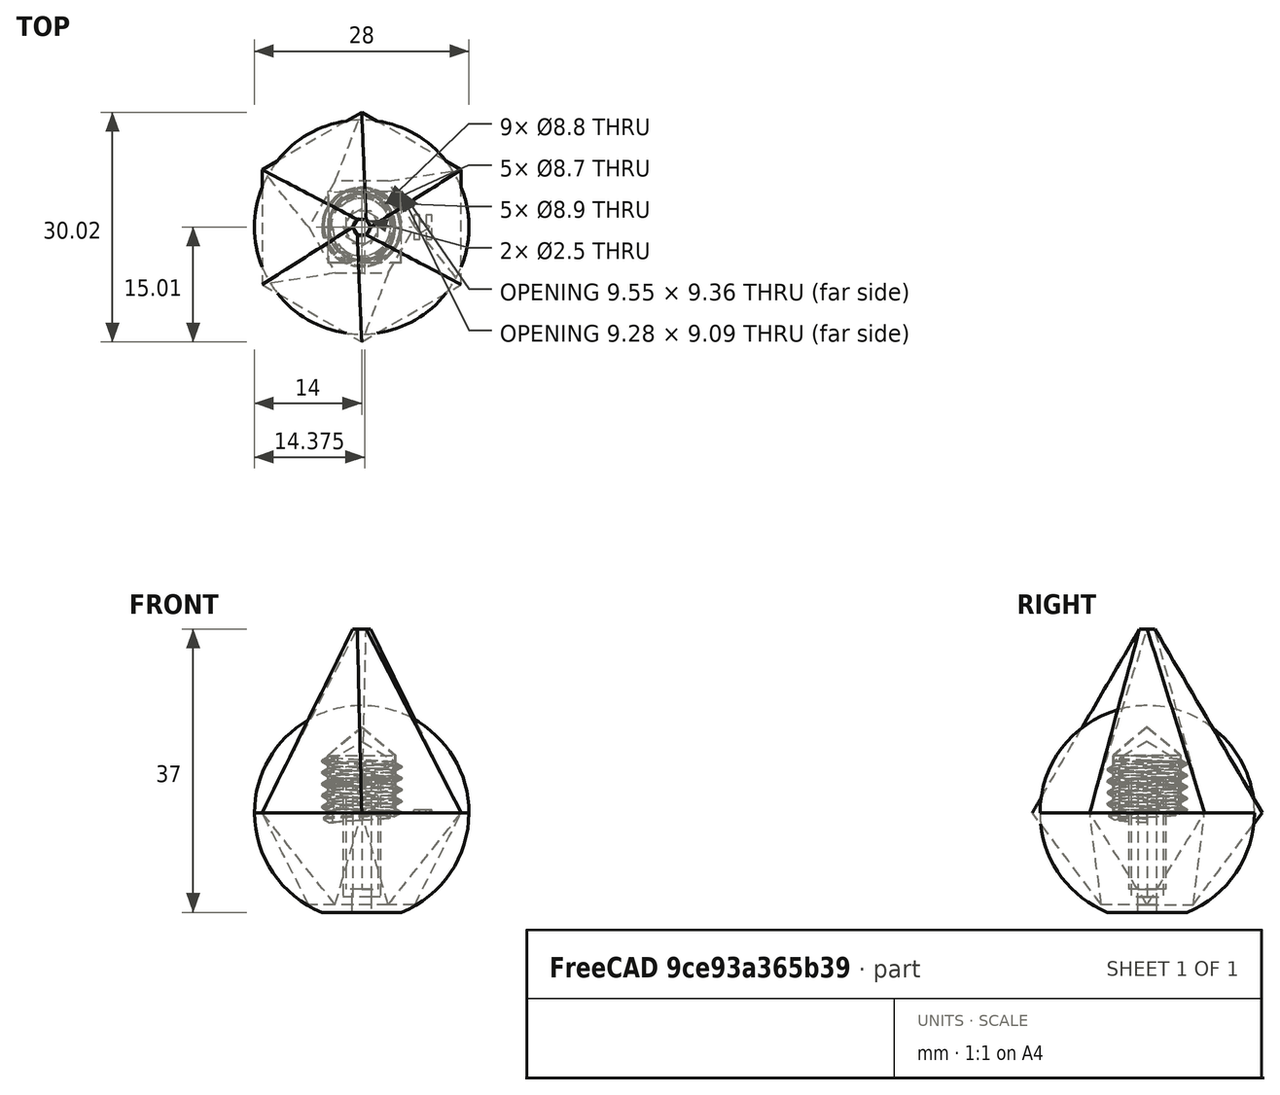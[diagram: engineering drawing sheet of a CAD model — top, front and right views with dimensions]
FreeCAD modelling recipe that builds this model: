
FCSTD DOCUMENT  (FreeCAD 2022.111R28429 (Git))
Label: Spec_PB3D_Tail_FCLinkBranch
License: All rights reserved
LicenseURL: http://en.wikipedia.org/wiki/All_rights_reserved
objects: Sketcher::SketchObject×23, PartDesign::Body×8, PartDesign::Hole×6, PartDesign::Pocket×6, PartDesign::Plane×4, PartDesign::AdditiveLoft×4, PartDesign::Revolution×2, PartDesign::Pad×2, PartDesign::SubShapeBinder×2, PartDesign::Boolean×2, PartDesign::Groove×2, App::Part×2, Mesh::Feature×2, Spreadsheet::Sheet×1
note: 107 computed .brp shape members not serialized (recipe doc carries the construction recipe); baked Part::Feature solids carry a one-line shape summary decoded from their .brp

FEATURE [Spreadsheet::Sheet] Spreadsheet  label="params"
  PythonMode = false
  ShowCells = 0
  TreeRank = 1
  cells = A1=M2 Bolt Clearances; C1=M2.5 Bolt Clearances; E1=Std Dims; G1=Clip; A2=Hole Clear Diam; B2(m2_hole_clear_diam)==2.5mm; C2=Hole Clear Diam; D2(m25_hole_clear_diam)==2.8mm; E2=Std. Chamfer; F2(std_chamf)==1mm; G2=Clip Tol; H2(clip_tol)==0.15mm; A3=Head Clear Diam; B3(m2_head_clear_diam)==4mm; C3=Head Clear Diam; D3(m25_head_clear_diam)==5mm; E3=Std. Radius; F3(std_rad)==2mm; A4=Head Min Depth; B4(m2_head_min_depth)==1.3mm; C4=Head Min Depth; D4(m25_head_min_depth)==1.6mm; G4=Clip Wall Thick; H4(clip_wall_thick)==0.8mm; A5=Nut Clear Flat; B5(m2_nut_clear_flat)==4.2mm; C5=Nut Clear Flat; D5(m25_nut_clear_flat)==5.2mm; G5=Clip Ball Diam; H5(clip_ball_diam)==0.5mm; A6=Nut Min Depth; B6(m2_nut_min_depth)==1.75mm; C6=Nut Min Depth; D6(m25_nut_min_depth)==2mm; G6=Clip Slot Width; H6(clip_slot_width)==clip_inner_diam / 2; G7=Clip Chamf; H7(clip_chamf)==1mm; A8=Tail Dims; C8=Base Plate Dims; A9=Tail Tot Height; B9(tail_tot_height)==tail_base_height + tail_top_height; C9=Base Plate Outer Diam; D9(base_plate_outer_diam)==9.4mm; G9=Clip Inner Diam; H9(clip_inner_diam)==5mm; A10=Tail Base Height; B10(tail_base_height)==12mm; C10=Base Plate Inner Diam; D10(base_plate_inner_diam)==4.8mm; G10=Clip Outer Diam; H10(clip_outer_diam)==clip_inner_diam + 2 * clip_wall_thick; A11=Tail Top Height; B11(tail_top_height)==24mm; C11=Base Plate Thick; D11(base_plate_thick)==1.2mm; G11=Clip Height; H11(clip_height)==clip_ball_diam + clip_chamf + 3mm; A12=Tail Base Width; B12(tail_base_width)==12mm; C12=Base Plate Groove Tol; D12(base_plate_groove_tol)==0.3mm; A13=Tail Mid Width; B13(tail_mid_width)==26mm; G13=Clip Width; H13(clip_width)==5mm; A14=Tail Top Width; B14(tail_top_width)==2mm; A16=Spring Wire Diam; B16(spring_wire_diam)==0.8mm; A18=Ball Tail Base Height; B18(balltail_base_height)==13mm; A19=Ball Tail Mid Rad; B19(balltail_mid_rad)==14mm; A20=Ball Tail Thread; B20(balltail_thread)==10mm; A21=Ball Tail Thread Height; B21(balltail_thread_height)==4.5mm
FEATURE [Sketcher::SketchObject] Sketch004  label="Sketch_RevTrimThread"
  FullyConstrained = true
  MapMode = 5
  Placement = pos=(0,0,0) rot=(0.57735,0.57735,0.57735;2.0944rad)
  Support = -> [YZ_Plane004]
  TreeRank = 36
  expr: Constraints[15] = Spec_PB3D_Tail_FCLinkBranch#<<params>>.balltail_thread_height * 1.5
  expr: Constraints[17] = Spec_PB3D_Tail_FCLinkBranch#<<params>>.balltail_thread_height
  expr: Constraints[18] = Spec_PB3D_Tail_FCLinkBranch#<<params>>.std_chamf
  expr: Constraints[20] = Spec_PB3D_Tail_FCLinkBranch#<<params>>.balltail_thread / 2
  sketch-geometry (7):
    g0: LineSegment StartX=0 StartY=4.5 StartZ=0 EndX=4 EndY=4.5 EndZ=0
    g1: LineSegment StartX=4 StartY=4.5 StartZ=0 EndX=5 EndY=3.5 EndZ=0
    g2: LineSegment StartX=5 StartY=3.5 StartZ=0 EndX=7 EndY=3.5 EndZ=0
    g3: LineSegment StartX=7 StartY=3.5 StartZ=0 EndX=7 EndY=11.25 EndZ=0
    g4: LineSegment StartX=7 StartY=11.25 StartZ=0 EndX=0 EndY=11.25 EndZ=0
    g5: LineSegment StartX=0 StartY=11.25 StartZ=0 EndX=0 EndY=4.5 EndZ=0
    g6: LineSegment [constr] StartX=4 StartY=4.5 StartZ=0 EndX=7 EndY=4.5 EndZ=0
  constraints (21):
    c: PointOnObject(g0,g-2)
    c: Horizontal(g0)
    c: Coincident(g1,g0)
    c: Coincident(g2,g1)
    c: Horizontal(g2)
    c: Coincident(g3,g2)
    c: Vertical(g3)
    c: Coincident(g4,g3)
    c: PointOnObject(g4,g-2)
    c: Horizontal(g4)
    c: Coincident(g5,g4)
    c: Coincident(g5,g0)
    c: Coincident(g6,g0)
    c: PointOnObject(g6,g3)
    c: Horizontal(g6)
    c: DistanceY(g5,g5) = 6.75
    c: Angle(g1,g6) = 0.785398
    c: DistanceY(g-1,g0) = 4.5
    c: DistanceY(g1,g0) = 1
    c: DistanceX(g2,g2) = 2
    c: DistanceX(g0,g1) = 5
FEATURE [Sketcher::SketchObject] Sketch005  label="Sketch_TailBallBase"
  FullyConstrained = true
  MapMode = 5
  Placement = pos=(0,0,0) rot=(1,0,0;1.5708rad)
  TreeRank = 38
  expr: Constraints[10] = Spec_PB3D_Tail_FCLinkBranch#<<params>>.balltail_mid_rad
  expr: Constraints[9] = Spec_PB3D_Tail_FCLinkBranch#<<params>>.balltail_base_height
  sketch-geometry (4):
    g0: LineSegment StartX=0 StartY=0 StartZ=0 EndX=14 EndY=0 EndZ=0
    g1: LineSegment StartX=0 StartY=0 StartZ=0 EndX=0 EndY=-13 EndZ=0
    g2: LineSegment StartX=0 StartY=-13 StartZ=0 EndX=5.19615 EndY=-13 EndZ=0
    g3: ArcOfCircle CenterX=0 CenterY=0 CenterZ=0 NormalX=0 NormalY=0 NormalZ=1 AngleXU=0 Radius=14 StartAngle=5.09264 EndAngle=6.28319
  constraints (11):
    c: Coincident(g0,g-1)
    c: Horizontal(g0)
    c: Coincident(g1,g0)
    c: Vertical(g1)
    c: Coincident(g2,g1)
    c: Horizontal(g2)
    c: Coincident(g3,g0)
    c: Coincident(g3,g0)
    c: Coincident(g3,g2)
    c: DistanceY(g1,g1) = 13
    c: DistanceX(g0,g0) = 14
FEATURE [PartDesign::Revolution] Revolution
  Angle = 360
  Axis = (0,0,1)
  Base = (0,0,0)
  ClaimChildren = false
  Fit = 0
  FitJoin = 0
  InnerFit = 0
  InnerFitJoin = 0
  NewSolid = false
  Placement = pos=(0,0,0) rot=(1,0,0;1.5708rad)
  Profile = -> Sketch005
  ReferenceAxis = -> Sketch005 [V_Axis]
  Reversed = true
  Suppress = false
  TreeRank = 52
  _ProfileBasedVersion = 1
FEATURE [Sketcher::SketchObject] Sketch  label="Sketch_M2HoleClear"
  FullyConstrained = true
  MapMode = 5
  Support = -> [XY_Plane004]
  TreeRank = 53
  expr: Constraints[1] = <<params>>.m2_hole_clear_diam
  sketch-geometry (1):
    g0: Circle CenterX=0 CenterY=0 CenterZ=0 NormalX=0 NormalY=0 NormalZ=1 AngleXU=0 Radius=1.25
  constraints (2):
    c: Coincident(g0,g-1)
    c: Diameter(g0) = 2.5
FEATURE [Sketcher::SketchObject] Sketch006  label="Sketch_M2NutHexSunk"
  FullyConstrained = true
  MapMode = 5
  Support = -> [XY_Plane004]
  TreeRank = 54
  expr: Constraints[19] = <<params>>.m2_nut_clear_flat
  sketch-geometry (7):
    g0: LineSegment StartX=2.42487 StartY=0 StartZ=0 EndX=1.21244 EndY=2.1 EndZ=0
    g1: LineSegment StartX=1.21244 StartY=2.1 StartZ=0 EndX=-1.21244 EndY=2.1 EndZ=0
    g2: LineSegment StartX=-1.21244 StartY=2.1 StartZ=0 EndX=-2.42487 EndY=4e-16 EndZ=0
    g3: LineSegment StartX=-2.42487 StartY=4e-16 StartZ=0 EndX=-1.21244 EndY=-2.1 EndZ=0
    g4: LineSegment StartX=-1.21244 StartY=-2.1 StartZ=0 EndX=1.21244 EndY=-2.1 EndZ=0
    g5: LineSegment StartX=1.21244 StartY=-2.1 StartZ=0 EndX=2.42487 EndY=0 EndZ=0
    g6: Circle [constr] CenterX=0 CenterY=0 CenterZ=0 NormalX=0 NormalY=0 NormalZ=1 AngleXU=0 Radius=2.42487
  constraints (16):
    c: Coincident(g0,g1)
    c: Coincident(g1,g2)
    c: Coincident(g2,g3)
    c: Coincident(g3,g4)
    c: Coincident(g4,g5)
    c: Coincident(g5,g0)
    c: Equal(g0, g1-g5) x5
    c: PointOnObject(g0,g6)
    c: PointOnObject(g1,g6)
    c: PointOnObject(g2,g6)
    c: PointOnObject(g3,g6)
    c: PointOnObject(g4,g6)
    c: PointOnObject(g5,g6)
    c: Coincident(g6,g-1)
    c: PointOnObject(g5,g-1)
    c: DistanceY(g4,g0) = 4.2
FEATURE [Sketcher::SketchObject] Sketch007  label="Sketch_ThreadPillar"
  FullyConstrained = true
  MapMode = 5
  Support = -> [XY_Plane005]
  TreeRank = 55
  expr: Constraints[1] = <<params>>.balltail_thread
  sketch-geometry (1):
    g0: Circle CenterX=0 CenterY=0 CenterZ=0 NormalX=0 NormalY=0 NormalZ=1 AngleXU=0 Radius=5
  constraints (2):
    c: Coincident(g0,g-1)
    c: Diameter(g0) = 10
FEATURE [PartDesign::Pad] Pad  label="Pad_ThreadPillar"
  ClaimChildren = false
  Direction = (1,1,1)
  Fit = 0
  FitJoin = 0
  InnerFit = 0
  InnerFitJoin = 0
  InnerTaperAngle = 0
  InnerTaperAngleRev = 0
  Length = 6.75
  Length2 = 100
  Linearize = true
  NewSolid = false
  Profile = -> Sketch007
  Suppress = false
  TreeRank = 56
  Type = 0
  _ProfileBasedVersion = 1
  expr: Length = <<params>>.balltail_thread_height * 1.5
FEATURE [PartDesign::Hole] Hole
  ClaimChildren = false
  CustomThreadClearance = 0
  Depth = 6.75
  DepthType = 0
  Diameter = 8.532
  DrillForDepth = false
  DrillPoint = 1
  DrillPointAngle = 118
  Fit = 0
  FitJoin = 0
  HoleCutCountersinkAngle = 90
  HoleCutCustomValues = false
  HoleCutDepth = 0
  HoleCutDiameter = 0
  HoleCutType = 0
  InnerFit = 0
  InnerFitJoin = 0
  ModelThread = true
  NewSolid = true
  Profile = -> Pad [Face2]
  Suppress = false
  Tapered = false
  TaperedAngle = 90
  ThreadClass = 0
  ThreadDepth = 6.75
  ThreadDepthType = 0
  ThreadDirection = 0
  ThreadFit = 0
  ThreadSize = 18
  ThreadType = 1
  Threaded = true
  TreeRank = 57
  UseCustomThreadClearance = false
  _ProfileBasedVersion = 1
  expr: Depth = <<params>>.balltail_thread_height * 1.5
FEATURE [PartDesign::Body] Body  label="ExtThread"
  AutoGroupSolids = false
  ExportMode = 0
  Group = -> [Sketch007,Pad,Hole]
  Origin = -> Origin005
  Tip = -> Hole
  TreeRank = 51
  _ExportChildren = -> [Pad,Hole]
  _GroupVersion = 1
FEATURE [PartDesign::SubShapeBinder] Reference  label="Reference(ExtThread)"
  BindCopyOnChange = 0
  BindMode = 0
  ClaimChildren = false
  Context = -> Part [Body003.Boolean.Reference.]
  FillStyle = 0
  Fuse = true
  MakeFace = true
  PartialLoad = false
  Relative = true
  Support = -> [Body]
  TreeRank = 59
  _Version = 8
FEATURE [PartDesign::Boolean] Boolean  label="Boolean_AddThread"
  BaseFeature = -> Revolution
  ExportMode = 0
  Group = -> [Reference]
  NewSolid = false
  Suppress = false
  TreeRank = 58
  Type = 0
  _ExportChildren = -> [Reference]
  _GroupVersion = 1
FEATURE [PartDesign::Groove] Groove  label="Groove_TrimThread"
  Angle = 360
  Axis = (-2e-16,3e-16,1)
  Base = (0,0,0)
  BaseFeature = -> Boolean
  ClaimChildren = false
  Fit = 0
  FitJoin = 0
  InnerFit = 0
  InnerFitJoin = 0
  NewSolid = false
  Profile = -> Sketch004
  ReferenceAxis = -> Sketch004 [V_Axis]
  Suppress = false
  TreeRank = 60
  _ProfileBasedVersion = 1
FEATURE [PartDesign::Pocket] Pocket  label="Pocket_M2ClearHole"
  BaseFeature = -> Groove
  ClaimChildren = false
  Fit = 0
  FitJoin = 0
  InnerFit = 0
  InnerFitJoin = 0
  InnerTaperAngle = 0
  InnerTaperAngleRev = 0
  Length = 5
  Length2 = 100
  Linearize = true
  Midplane = true
  NewSolid = false
  Profile = -> Sketch
  Suppress = false
  TreeRank = 61
  Type = 1
  _ProfileBasedVersion = 1
FEATURE [PartDesign::Pocket] Pocket001  label="Pocket_HexSunk"
  BaseFeature = -> Pocket
  ClaimChildren = false
  Fit = 0
  FitJoin = 0
  InnerFit = 0
  InnerFitJoin = 0
  InnerTaperAngle = 0
  InnerTaperAngleRev = 0
  Length = 11
  Length2 = 100
  Linearize = true
  NewSolid = false
  Profile = -> Sketch006
  Suppress = false
  TreeRank = 62
  Type = 4
  _ProfileBasedVersion = 1
  expr: Length = <<params>>.balltail_base_height - 2mm
FEATURE [PartDesign::Body] Body003  label="Ball_Tail_Base"
  AutoGroupSolids = false
  ExportMode = 0
  Group = -> [Sketch004,Sketch005,Revolution,Sketch,Sketch006,Boolean,Groove,Pocket,Pocket001]
  Origin = -> Origin004
  Tip = -> Pocket001
  TreeRank = 41
  _ExportChildren = -> [Revolution,Boolean,Groove,Pocket,Pocket001]
  _GroupVersion = 1
FEATURE [Sketcher::SketchObject] Sketch008  label="Sketch_BallTailTop"
  FullyConstrained = true
  MapMode = 5
  Placement = pos=(0,0,0) rot=(1,0,0;1.5708rad)
  Support = -> [XZ_Plane006]
  TreeRank = 73
  expr: Constraints[7] = <<params>>.balltail_mid_rad
  sketch-geometry (3):
    g0: ArcOfCircle CenterX=1.8e-15 CenterY=0 CenterZ=0 NormalX=0 NormalY=0 NormalZ=1 AngleXU=0 Radius=14 StartAngle=0 EndAngle=1.5708
    g1: LineSegment StartX=1.8e-15 StartY=0 StartZ=0 EndX=1.8e-15 EndY=14 EndZ=0
    g2: LineSegment StartX=1.8e-15 StartY=0 StartZ=0 EndX=14 EndY=0 EndZ=0
  constraints (8):
    c: Coincident(g0,g-1)
    c: PointOnObject(g0,g-1)
    c: Coincident(g1,g0)
    c: Coincident(g1,g0)
    c: Vertical(g1)
    c: Coincident(g2,g0)
    c: Coincident(g2,g0)
    c: DistanceY(g1,g1) = 14
FEATURE [PartDesign::Revolution] Revolution001
  Angle = 360
  Axis = (0,-2e-16,1)
  Base = (0,0,0)
  ClaimChildren = false
  Fit = 0
  FitJoin = 0
  InnerFit = 0
  InnerFitJoin = 0
  NewSolid = false
  Placement = pos=(0,0,0) rot=(1,0,0;1.5708rad)
  Profile = -> Sketch008
  ReferenceAxis = -> Sketch008 [V_Axis]
  Reversed = true
  Suppress = false
  TreeRank = 74
  _ProfileBasedVersion = 1
FEATURE [PartDesign::Hole] Hole001
  BaseFeature = -> Revolution001
  ClaimChildren = false
  CustomThreadClearance = 0.3
  Depth = 7.5
  DepthType = 0
  Diameter = 8.8
  DrillForDepth = false
  DrillPoint = 1
  DrillPointAngle = 100
  Fit = 0
  FitJoin = 0
  HoleCutCountersinkAngle = 90
  HoleCutCustomValues = false
  HoleCutDepth = 0
  HoleCutDiameter = 8.9
  HoleCutType = 0
  InnerFit = 0
  InnerFitJoin = 0
  ModelThread = true
  NewSolid = false
  Placement = pos=(0,0,0) rot=(1,0,0;1.5708rad)
  Profile = -> Revolution001 [Face2]
  Suppress = false
  Tapered = false
  TaperedAngle = 90
  ThreadClass = 0
  ThreadDepth = 7.5
  ThreadDepthType = 0
  ThreadDirection = 0
  ThreadFit = 0
  ThreadSize = 18
  ThreadType = 1
  Threaded = true
  TreeRank = 75
  UseCustomThreadClearance = true
  _ProfileBasedVersion = 1
  expr: Depth = <<params>>.balltail_thread_height + 2 * 1.5mm
FEATURE [PartDesign::Body] Body004  label="Ball_Tail_Top"
  AutoGroupSolids = false
  ExportMode = 0
  Group = -> [Sketch008,Revolution001,Hole001]
  Origin = -> Origin006
  Tip = -> Hole001
  TreeRank = 72
  _ExportChildren = -> [Revolution001,Hole001]
  _GroupVersion = 1
FEATURE [App::Part] Part  label="Balll_Tail_Part"
  ExportMode = 1
  Group = -> [Body003,Body,Body004]
  Origin = -> Origin
  TreeRank = 1
  _ExportChildren = -> [Body003,Body,Body004]
  _GroupVersion = 1
FEATURE [PartDesign::Plane] DatumPlane  label="Datum_HexBase"
  AttachmentOffset = pos=(0,0,-12) rot=(0,0,1;0rad)
  Length = 26
  MapMode = 5
  MinimumLength = 10
  MinimumWidth = 10
  Placement = pos=(0,0,-12) rot=(0,0,1;0rad)
  ResizeMode = 0
  Support = -> [XY_Plane007]
  TreeRank = 90
  Width = 30.0222
  expr: AttachmentOffset.Base.z = <<params>>.tail_base_height * -1
FEATURE [Sketcher::SketchObject] Sketch009  label="Tail_Hex_Mid"
  FullyConstrained = true
  MapMode = 5
  Support = -> [XY_Plane007]
  TreeRank = 91
  expr: Constraints[19] = <<params>>.tail_mid_width
  sketch-geometry (7):
    g0: LineSegment StartX=0 StartY=15.0111 StartZ=0 EndX=-13 EndY=7.50555 EndZ=0
    g1: LineSegment StartX=-13 StartY=7.50555 StartZ=0 EndX=-13 EndY=-7.50555 EndZ=0
    g2: LineSegment StartX=-13 StartY=-7.50555 StartZ=0 EndX=0 EndY=-15.0111 EndZ=0
    g3: LineSegment StartX=4e-16 StartY=-15.0111 StartZ=0 EndX=13 EndY=-7.50555 EndZ=0
    g4: LineSegment StartX=13 StartY=-7.50555 StartZ=0 EndX=13 EndY=7.50555 EndZ=0
    g5: LineSegment StartX=13 StartY=7.50555 StartZ=0 EndX=0 EndY=15.0111 EndZ=0
    g6: Circle [constr] CenterX=0 CenterY=0 CenterZ=0 NormalX=0 NormalY=0 NormalZ=1 AngleXU=0 Radius=15.0111
  constraints (16):
    c: Coincident(g0,g1)
    c: Coincident(g1,g2)
    c: Coincident(g2,g3)
    c: Coincident(g3,g4)
    c: Coincident(g4,g5)
    c: Coincident(g5,g0)
    c: Equal(g0, g1-g5) x5
    c: PointOnObject(g0,g6)
    c: PointOnObject(g1,g6)
    c: PointOnObject(g2,g6)
    c: PointOnObject(g3,g6)
    c: PointOnObject(g4,g6)
    c: PointOnObject(g5,g6)
    c: Coincident(g6,g-1)
    c: PointOnObject(g5,g-2)
    c: DistanceX(g0,g4) = 26
FEATURE [Sketcher::SketchObject] Sketch010  label="Tail_Hex_Base"
  FullyConstrained = true
  MapMode = 5
  Placement = pos=(0,0,-12) rot=(0,0,1;0rad)
  Support = -> [DatumPlane]
  TreeRank = 92
  expr: Constraints[19] = <<params>>.tail_base_width
  sketch-geometry (7):
    g0: LineSegment StartX=6.9282 StartY=0 StartZ=0 EndX=3.4641 EndY=6 EndZ=0
    g1: LineSegment StartX=3.4641 StartY=6 StartZ=0 EndX=-3.4641 EndY=6 EndZ=0
    g2: LineSegment StartX=-3.4641 StartY=6 StartZ=0 EndX=-6.9282 EndY=2.38698e-11 EndZ=0
    g3: LineSegment StartX=-6.9282 StartY=2.38698e-11 StartZ=0 EndX=-3.4641 EndY=-6 EndZ=0
    g4: LineSegment StartX=-3.4641 StartY=-6 StartZ=0 EndX=3.4641 EndY=-6 EndZ=0
    g5: LineSegment StartX=3.4641 StartY=-6 StartZ=0 EndX=6.9282 EndY=0 EndZ=0
    g6: Circle [constr] CenterX=0 CenterY=0 CenterZ=0 NormalX=0 NormalY=0 NormalZ=1 AngleXU=0 Radius=6.9282
  constraints (16):
    c: Coincident(g0,g1)
    c: Coincident(g1,g2)
    c: Coincident(g2,g3)
    c: Coincident(g3,g4)
    c: Coincident(g4,g5)
    c: Coincident(g5,g0)
    c: Equal(g0, g1-g5) x5
    c: PointOnObject(g0,g6)
    c: PointOnObject(g1,g6)
    c: PointOnObject(g2,g6)
    c: PointOnObject(g3,g6)
    c: PointOnObject(g4,g6)
    c: PointOnObject(g5,g6)
    c: Coincident(g6,g-1)
    c: PointOnObject(g5,g-1)
    c: DistanceY(g4,g0) = 12
FEATURE [Sketcher::SketchObject] Sketch011  label="Sketch_ThreadPillar001"
  FullyConstrained = true
  MapMode = 5
  Support = -> [XY_Plane008]
  TreeRank = 55
  expr: Constraints[1] = Spec_PB3D_Tail_FCLinkBranch#<<params>>.balltail_thread
  sketch-geometry (1):
    g0: Circle CenterX=0 CenterY=0 CenterZ=0 NormalX=0 NormalY=0 NormalZ=1 AngleXU=0 Radius=5
  constraints (2):
    c: Coincident(g0,g-1)
    c: Diameter(g0) = 10
FEATURE [PartDesign::Pad] Pad001  label="Pad_ThreadPillar001"
  ClaimChildren = false
  Direction = (1,1,1)
  Fit = 0
  FitJoin = 0
  InnerFit = 0
  InnerFitJoin = 0
  InnerTaperAngle = 0
  InnerTaperAngleRev = 0
  Length = 6.75
  Length2 = 100
  Linearize = true
  NewSolid = false
  Profile = -> Sketch011
  Suppress = false
  TreeRank = 56
  Type = 0
  _ProfileBasedVersion = 1
  expr: Length = Spec_PB3D_Tail_FCLinkBranch#<<params>>.balltail_thread_height * 1.5
FEATURE [PartDesign::Hole] Hole002
  ClaimChildren = false
  CustomThreadClearance = 0
  Depth = 6.75
  DepthType = 0
  Diameter = 8.532
  DrillForDepth = false
  DrillPoint = 1
  DrillPointAngle = 118
  Fit = 0
  FitJoin = 0
  HoleCutCountersinkAngle = 90
  HoleCutCustomValues = false
  HoleCutDepth = 0
  HoleCutDiameter = 0
  HoleCutType = 0
  InnerFit = 0
  InnerFitJoin = 0
  ModelThread = true
  NewSolid = true
  Profile = -> Pad001 [Face2]
  Suppress = false
  Tapered = false
  TaperedAngle = 90
  ThreadClass = 0
  ThreadDepth = 6.75
  ThreadDepthType = 0
  ThreadDirection = 0
  ThreadFit = 0
  ThreadSize = 18
  ThreadType = 1
  Threaded = true
  TreeRank = 57
  UseCustomThreadClearance = false
  _ProfileBasedVersion = 1
  expr: Depth = Spec_PB3D_Tail_FCLinkBranch#<<params>>.balltail_thread_height * 1.5
FEATURE [PartDesign::Body] Body006  label="ExtThread001"
  AutoGroupSolids = false
  ExportMode = 0
  Group = -> [Sketch011,Pad001,Hole002]
  Origin = -> Origin009
  Tip = -> Hole002
  TreeRank = 93
  _ExportChildren = -> [Pad001,Hole002]
  _GroupVersion = 1
FEATURE [PartDesign::AdditiveLoft] AdditiveLoft  label="AddLoft_HexBase"
  ClaimChildren = false
  Closed = false
  Fit = 0
  FitJoin = 0
  InnerFit = 0
  InnerFitJoin = 0
  NewSolid = false
  Placement = pos=(0,0,-12) rot=(0,0,1;0rad)
  Profile = -> Sketch010
  Ruled = false
  Sections = -> [Sketch009]
  Suppress = false
  TreeRank = 94
  _ProfileBasedVersion = 1
FEATURE [Sketcher::SketchObject] Sketch012  label="Sketch_M2_ClearHole"
  FullyConstrained = true
  MapMode = 5
  Support = -> [XY_Plane007]
  TreeRank = 107
  expr: Constraints[1] = <<params>>.m2_hole_clear_diam
  sketch-geometry (1):
    g0: Circle CenterX=0 CenterY=0 CenterZ=0 NormalX=0 NormalY=0 NormalZ=1 AngleXU=0 Radius=1.25
  constraints (2):
    c: Coincident(g0,g-1)
    c: Diameter(g0) = 2.5
FEATURE [Sketcher::SketchObject] Sketch013  label="Sketch_M2_HexSunk"
  FullyConstrained = true
  MapMode = 5
  Support = -> [XY_Plane007]
  TreeRank = 109
  expr: Constraints[19] = <<params>>.m2_nut_clear_flat
  sketch-geometry (7):
    g0: LineSegment StartX=0 StartY=2.42487 StartZ=0 EndX=-2.1 EndY=1.21244 EndZ=0
    g1: LineSegment StartX=-2.1 StartY=1.21244 StartZ=0 EndX=-2.1 EndY=-1.21244 EndZ=0
    g2: LineSegment StartX=-2.1 StartY=-1.21244 StartZ=0 EndX=-5.791e-13 EndY=-2.42487 EndZ=0
    g3: LineSegment StartX=-5.791e-13 StartY=-2.42487 StartZ=0 EndX=2.1 EndY=-1.21244 EndZ=0
    g4: LineSegment StartX=2.1 StartY=-1.21244 StartZ=0 EndX=2.1 EndY=1.21244 EndZ=0
    g5: LineSegment StartX=2.1 StartY=1.21244 StartZ=0 EndX=0 EndY=2.42487 EndZ=0
    g6: Circle [constr] CenterX=0 CenterY=0 CenterZ=0 NormalX=0 NormalY=0 NormalZ=1 AngleXU=0 Radius=2.42487
  constraints (16):
    c: Coincident(g0,g1)
    c: Coincident(g1,g2)
    c: Coincident(g2,g3)
    c: Coincident(g3,g4)
    c: Coincident(g4,g5)
    c: Coincident(g5,g0)
    c: Equal(g0, g1-g5) x5
    c: PointOnObject(g0,g6)
    c: PointOnObject(g1,g6)
    c: PointOnObject(g2,g6)
    c: PointOnObject(g3,g6)
    c: PointOnObject(g4,g6)
    c: PointOnObject(g5,g6)
    c: Coincident(g6,g-1)
    c: PointOnObject(g5,g-2)
    c: DistanceX(g0,g4) = 4.2
FEATURE [PartDesign::SubShapeBinder] Reference001  label="Reference001(ExtThread001)"
  BindCopyOnChange = 0
  BindMode = 0
  ClaimChildren = false
  Context = -> Part001 [Body005.Boolean001.Reference001.]
  FillStyle = 0
  Fuse = true
  MakeFace = true
  PartialLoad = false
  Relative = true
  Support = -> [Body006]
  TreeRank = 111
  _Version = 8
FEATURE [PartDesign::Boolean] Boolean001  label="Boolean_AddThread001"
  BaseFeature = -> AdditiveLoft
  ExportMode = 0
  Group = -> [Reference001]
  NewSolid = false
  Suppress = false
  TreeRank = 110
  Type = 0
  _ExportChildren = -> [Reference001]
  _GroupVersion = 1
FEATURE [Sketcher::SketchObject] Sketch014  label="Sketch_RevTrimThread001"
  FullyConstrained = true
  MapMode = 5
  Placement = pos=(0,0,0) rot=(0.57735,0.57735,0.57735;2.0944rad)
  Support = -> [YZ_Plane007]
  TreeRank = 112
  expr: Constraints[15] = Spec_PB3D_Tail_FCLinkBranch#<<params>>.balltail_thread_height * 1.5
  expr: Constraints[17] = Spec_PB3D_Tail_FCLinkBranch#<<params>>.balltail_thread_height
  expr: Constraints[18] = Spec_PB3D_Tail_FCLinkBranch#<<params>>.std_chamf
  expr: Constraints[20] = Spec_PB3D_Tail_FCLinkBranch#<<params>>.balltail_thread / 2
  sketch-geometry (7):
    g0: LineSegment StartX=0 StartY=4.5 StartZ=0 EndX=4 EndY=4.5 EndZ=0
    g1: LineSegment StartX=4 StartY=4.5 StartZ=0 EndX=5 EndY=3.5 EndZ=0
    g2: LineSegment StartX=5 StartY=3.5 StartZ=0 EndX=7 EndY=3.5 EndZ=0
    g3: LineSegment StartX=7 StartY=3.5 StartZ=0 EndX=7 EndY=11.25 EndZ=0
    g4: LineSegment StartX=7 StartY=11.25 StartZ=0 EndX=0 EndY=11.25 EndZ=0
    g5: LineSegment StartX=0 StartY=11.25 StartZ=0 EndX=0 EndY=4.5 EndZ=0
    g6: LineSegment [constr] StartX=4 StartY=4.5 StartZ=0 EndX=7 EndY=4.5 EndZ=0
  constraints (21):
    c: PointOnObject(g0,g-2)
    c: Horizontal(g0)
    c: Coincident(g1,g0)
    c: Coincident(g2,g1)
    c: Horizontal(g2)
    c: Coincident(g3,g2)
    c: Vertical(g3)
    c: Coincident(g4,g3)
    c: PointOnObject(g4,g-2)
    c: Horizontal(g4)
    c: Coincident(g5,g4)
    c: Coincident(g5,g0)
    c: Coincident(g6,g0)
    c: PointOnObject(g6,g3)
    c: Horizontal(g6)
    c: DistanceY(g5,g5) = 6.75
    c: Angle(g1,g6) = 0.785398
    c: DistanceY(g-1,g0) = 4.5
    c: DistanceY(g1,g0) = 1
    c: DistanceX(g2,g2) = 2
    c: DistanceX(g0,g1) = 5
FEATURE [PartDesign::Groove] Groove001  label="Groove_TrimThread001"
  Angle = 360
  Axis = (-2e-16,3e-16,1)
  Base = (0,0,0)
  BaseFeature = -> Boolean001
  ClaimChildren = false
  Fit = 0
  FitJoin = 0
  InnerFit = 0
  InnerFitJoin = 0
  NewSolid = false
  Profile = -> Sketch014
  ReferenceAxis = -> Sketch014 [V_Axis]
  Suppress = false
  TreeRank = 113
  _ProfileBasedVersion = 1
FEATURE [PartDesign::Pocket] Pocket002  label="Pocket_M2Hole"
  BaseFeature = -> Groove001
  ClaimChildren = false
  Fit = 0
  FitJoin = 0
  InnerFit = 0
  InnerFitJoin = 0
  InnerTaperAngle = 0
  InnerTaperAngleRev = 0
  Length = 5
  Length2 = 100
  Linearize = true
  Midplane = true
  NewSolid = false
  Profile = -> Sketch012
  Suppress = false
  TreeRank = 114
  Type = 1
  _ProfileBasedVersion = 1
FEATURE [PartDesign::Pocket] Pocket003  label="Pocket_HexSunk001"
  BaseFeature = -> Pocket002
  ClaimChildren = false
  Fit = 0
  FitJoin = 0
  InnerFit = 0
  InnerFitJoin = 0
  InnerTaperAngle = 0
  InnerTaperAngleRev = 0
  Length = 10
  Length2 = 100
  Linearize = true
  NewSolid = false
  Profile = -> Sketch013
  Suppress = false
  TreeRank = 115
  Type = 4
  _ProfileBasedVersion = 1
  expr: Length = <<params>>.tail_base_height - 2mm
FEATURE [PartDesign::Body] Body005  label="Hex_Tail_Base"
  AutoGroupSolids = false
  ExportMode = 0
  Group = -> [DatumPlane,Sketch009,Sketch010,AdditiveLoft,Sketch012,Sketch013,Boolean001,Sketch014,Groove001,Pocket002,Pocket003]
  Origin = -> Origin008
  Tip = -> Pocket003
  TreeRank = 89
  _ExportChildren = -> [DatumPlane,AdditiveLoft,Boolean001,Groove001,Pocket002,Pocket003]
  _GroupVersion = 1
FEATURE [Sketcher::SketchObject] Sketch015  label="Sketch_TailMid"
  FullyConstrained = true
  MapMode = 5
  Support = -> [XY_Plane010]
  TreeRank = 126
  expr: Constraints[19] = <<params>>.tail_mid_width
  sketch-geometry (7):
    g0: LineSegment StartX=0 StartY=-15.0111 StartZ=0 EndX=13 EndY=-7.50555 EndZ=0
    g1: LineSegment StartX=13 StartY=-7.50555 StartZ=0 EndX=13 EndY=7.50555 EndZ=0
    g2: LineSegment StartX=13 StartY=7.50555 StartZ=0 EndX=0 EndY=15.0111 EndZ=0
    g3: LineSegment StartX=-8e-16 StartY=15.0111 StartZ=0 EndX=-13 EndY=7.50555 EndZ=0
    g4: LineSegment StartX=-13 StartY=7.50555 StartZ=0 EndX=-13 EndY=-7.50555 EndZ=0
    g5: LineSegment StartX=-13 StartY=-7.50555 StartZ=0 EndX=0 EndY=-15.0111 EndZ=0
    g6: Circle [constr] CenterX=0 CenterY=0 CenterZ=0 NormalX=0 NormalY=0 NormalZ=1 AngleXU=0 Radius=15.0111
  constraints (16):
    c: Coincident(g0,g1)
    c: Coincident(g1,g2)
    c: Coincident(g2,g3)
    c: Coincident(g3,g4)
    c: Coincident(g4,g5)
    c: Coincident(g5,g0)
    c: Equal(g0, g1-g5) x5
    c: PointOnObject(g0,g6)
    c: PointOnObject(g1,g6)
    c: PointOnObject(g2,g6)
    c: PointOnObject(g3,g6)
    c: PointOnObject(g4,g6)
    c: PointOnObject(g5,g6)
    c: Coincident(g6,g-1)
    c: PointOnObject(g5,g-2)
    c: DistanceX(g3,g1) = 26
FEATURE [PartDesign::Plane] DatumPlane001  label="DatumPlane_TailTop"
  AttachmentOffset = pos=(0,0,24) rot=(0,0,1;0rad)
  Length = 26
  MapMode = 5
  MinimumLength = 10
  MinimumWidth = 10
  Placement = pos=(0,0,24) rot=(0,0,1;0rad)
  ResizeMode = 0
  Support = -> [XY_Plane010]
  TreeRank = 127
  Width = 30.0222
  expr: AttachmentOffset.Base.z = <<params>>.tail_top_height
FEATURE [Sketcher::SketchObject] Sketch016  label="Sketch_TailTop"
  FullyConstrained = true
  MapMode = 5
  Placement = pos=(0,0,24) rot=(0,0,1;0rad)
  Support = -> [DatumPlane001]
  TreeRank = 128
  expr: Constraints[19] = <<params>>.tail_top_width
  sketch-geometry (7):
    g0: LineSegment StartX=1.1547 StartY=1e-16 StartZ=0 EndX=0.57735 EndY=1 EndZ=0
    g1: LineSegment StartX=0.57735 StartY=1 StartZ=0 EndX=-0.57735 EndY=1 EndZ=0
    g2: LineSegment StartX=-0.57735 StartY=1 StartZ=0 EndX=-1.1547 EndY=-1.1e-15 EndZ=0
    g3: LineSegment StartX=-1.1547 StartY=-1.1e-15 StartZ=0 EndX=-0.57735 EndY=-1 EndZ=0
    g4: LineSegment StartX=-0.57735 StartY=-1 StartZ=0 EndX=0.57735 EndY=-1 EndZ=0
    g5: LineSegment StartX=0.57735 StartY=-1 StartZ=0 EndX=1.1547 EndY=1e-16 EndZ=0
    g6: Circle [constr] CenterX=0 CenterY=0 CenterZ=0 NormalX=0 NormalY=0 NormalZ=1 AngleXU=0 Radius=1.1547
  constraints (16):
    c: Coincident(g0,g1)
    c: Coincident(g1,g2)
    c: Coincident(g2,g3)
    c: Coincident(g3,g4)
    c: Coincident(g4,g5)
    c: Coincident(g5,g0)
    c: Equal(g0, g1-g5) x5
    c: PointOnObject(g0,g6)
    c: PointOnObject(g1,g6)
    c: PointOnObject(g2,g6)
    c: PointOnObject(g3,g6)
    c: PointOnObject(g4,g6)
    c: PointOnObject(g5,g6)
    c: Coincident(g6,g-1)
    c: PointOnObject(g5,g-1)
    c: DistanceY(g4,g0) = 2
FEATURE [PartDesign::AdditiveLoft] AdditiveLoft001  label="AddLoft_HexTail_Top"
  ClaimChildren = false
  Closed = false
  Fit = 0
  FitJoin = 0
  InnerFit = 0
  InnerFitJoin = 0
  NewSolid = false
  Profile = -> Sketch015
  Ruled = false
  Sections = -> [Sketch016]
  Suppress = false
  TreeRank = 129
  _ProfileBasedVersion = 1
FEATURE [Sketcher::SketchObject] Sketch017  label="Sketch_HoleLock"
  FullyConstrained = true
  MapMode = 5
  Support = -> [XY_Plane010]
  TreeRank = 130
  expr: Constraints[1] = <<params>>.m2_hole_clear_diam
  sketch-geometry (1):
    g0: Circle CenterX=0 CenterY=0 CenterZ=0 NormalX=0 NormalY=0 NormalZ=1 AngleXU=0 Radius=1.25
  constraints (2):
    c: Coincident(g0,g-1)
    c: Diameter(g0) = 2.5
FEATURE [PartDesign::Hole] Hole003  label="Hole_InternThread"
  BaseFeature = -> AdditiveLoft001
  ClaimChildren = false
  CustomThreadClearance = 0.4
  Depth = 7.5
  DepthType = 0
  Diameter = 8.9
  DrillForDepth = false
  DrillPoint = 1
  DrillPointAngle = 100
  Fit = 0
  FitJoin = 0
  HoleCutCountersinkAngle = 90
  HoleCutCustomValues = false
  HoleCutDepth = 0
  HoleCutDiameter = 9
  HoleCutType = 0
  InnerFit = 0
  InnerFitJoin = 0
  ModelThread = true
  NewSolid = false
  Profile = -> Sketch017
  Reversed = true
  Suppress = false
  Tapered = false
  TaperedAngle = 90
  ThreadClass = 0
  ThreadDepth = 7.5
  ThreadDepthType = 0
  ThreadDirection = 0
  ThreadFit = 0
  ThreadSize = 18
  ThreadType = 1
  Threaded = true
  TreeRank = 131
  UseCustomThreadClearance = true
  _ProfileBasedVersion = 1
  expr: Depth = <<params>>.balltail_thread_height + 2 * 1.5mm
FEATURE [PartDesign::Body] Body007  label="Hex_Tail_Top_Tol04mm"
  AutoGroupSolids = false
  ExportMode = 0
  Group = -> [Sketch015,DatumPlane001,Sketch016,AdditiveLoft001,Sketch017,Hole003]
  Origin = -> Origin010
  Tip = -> Hole003
  TreeRank = 125
  _ExportChildren = -> [DatumPlane001,AdditiveLoft001,Hole003]
  _GroupVersion = 1
FEATURE [PartDesign::Plane] DatumPlane002  label="DatumPlane_TailTop001"
  AttachmentOffset = pos=(0,0,24) rot=(0,0,1;0rad)
  Length = 26
  MapMode = 5
  MinimumLength = 10
  MinimumWidth = 10
  Placement = pos=(0,0,24) rot=(0,0,1;0rad)
  ResizeMode = 0
  Support = -> [XY_Plane011]
  TreeRank = 127
  Width = 30.0222
  expr: AttachmentOffset.Base.z = Spec_PB3D_Tail_FCLinkBranch#<<params>>.tail_top_height
FEATURE [Sketcher::SketchObject] Sketch018  label="Sketch_TailMid001"
  FullyConstrained = true
  MapMode = 5
  Support = -> [XY_Plane011]
  TreeRank = 126
  expr: Constraints[19] = Spec_PB3D_Tail_FCLinkBranch#<<params>>.tail_mid_width
  sketch-geometry (7):
    g0: LineSegment StartX=0 StartY=-15.0111 StartZ=0 EndX=13 EndY=-7.50555 EndZ=0
    g1: LineSegment StartX=13 StartY=-7.50555 StartZ=0 EndX=13 EndY=7.50555 EndZ=0
    g2: LineSegment StartX=13 StartY=7.50555 StartZ=0 EndX=0 EndY=15.0111 EndZ=0
    g3: LineSegment StartX=-8e-16 StartY=15.0111 StartZ=0 EndX=-13 EndY=7.50555 EndZ=0
    g4: LineSegment StartX=-13 StartY=7.50555 StartZ=0 EndX=-13 EndY=-7.50555 EndZ=0
    g5: LineSegment StartX=-13 StartY=-7.50555 StartZ=0 EndX=0 EndY=-15.0111 EndZ=0
    g6: Circle [constr] CenterX=0 CenterY=0 CenterZ=0 NormalX=0 NormalY=0 NormalZ=1 AngleXU=0 Radius=15.0111
  constraints (16):
    c: Coincident(g0,g1)
    c: Coincident(g1,g2)
    c: Coincident(g2,g3)
    c: Coincident(g3,g4)
    c: Coincident(g4,g5)
    c: Coincident(g5,g0)
    c: Equal(g0, g1-g5) x5
    c: PointOnObject(g0,g6)
    c: PointOnObject(g1,g6)
    c: PointOnObject(g2,g6)
    c: PointOnObject(g3,g6)
    c: PointOnObject(g4,g6)
    c: PointOnObject(g5,g6)
    c: Coincident(g6,g-1)
    c: PointOnObject(g5,g-2)
    c: DistanceX(g3,g1) = 26
FEATURE [Sketcher::SketchObject] Sketch019  label="Sketch_TailTop001"
  FullyConstrained = true
  MapMode = 5
  Placement = pos=(0,0,24) rot=(0,0,1;0rad)
  Support = -> [DatumPlane002]
  TreeRank = 128
  expr: Constraints[19] = Spec_PB3D_Tail_FCLinkBranch#<<params>>.tail_top_width
  sketch-geometry (7):
    g0: LineSegment StartX=1.1547 StartY=1e-16 StartZ=0 EndX=0.57735 EndY=1 EndZ=0
    g1: LineSegment StartX=0.57735 StartY=1 StartZ=0 EndX=-0.57735 EndY=1 EndZ=0
    g2: LineSegment StartX=-0.57735 StartY=1 StartZ=0 EndX=-1.1547 EndY=-1.1e-15 EndZ=0
    g3: LineSegment StartX=-1.1547 StartY=-1.1e-15 StartZ=0 EndX=-0.57735 EndY=-1 EndZ=0
    g4: LineSegment StartX=-0.57735 StartY=-1 StartZ=0 EndX=0.57735 EndY=-1 EndZ=0
    g5: LineSegment StartX=0.57735 StartY=-1 StartZ=0 EndX=1.1547 EndY=1e-16 EndZ=0
    g6: Circle [constr] CenterX=0 CenterY=0 CenterZ=0 NormalX=0 NormalY=0 NormalZ=1 AngleXU=0 Radius=1.1547
  constraints (16):
    c: Coincident(g0,g1)
    c: Coincident(g1,g2)
    c: Coincident(g2,g3)
    c: Coincident(g3,g4)
    c: Coincident(g4,g5)
    c: Coincident(g5,g0)
    c: Equal(g0, g1-g5) x5
    c: PointOnObject(g0,g6)
    c: PointOnObject(g1,g6)
    c: PointOnObject(g2,g6)
    c: PointOnObject(g3,g6)
    c: PointOnObject(g4,g6)
    c: PointOnObject(g5,g6)
    c: Coincident(g6,g-1)
    c: PointOnObject(g5,g-1)
    c: DistanceY(g4,g0) = 2
FEATURE [PartDesign::AdditiveLoft] AdditiveLoft002  label="AddLoft_HexTail_Top001"
  ClaimChildren = false
  Closed = false
  Fit = 0
  FitJoin = 0
  InnerFit = 0
  InnerFitJoin = 0
  NewSolid = false
  Profile = -> Sketch018
  Ruled = false
  Sections = -> [Sketch019]
  Suppress = false
  TreeRank = 132
  _ProfileBasedVersion = 1
FEATURE [Sketcher::SketchObject] Sketch020  label="Sketch_HoleLock001"
  FullyConstrained = true
  MapMode = 5
  Support = -> [XY_Plane011]
  TreeRank = 130
  expr: Constraints[1] = Spec_PB3D_Tail_FCLinkBranch#<<params>>.m2_hole_clear_diam
  sketch-geometry (1):
    g0: Circle CenterX=0 CenterY=0 CenterZ=0 NormalX=0 NormalY=0 NormalZ=1 AngleXU=0 Radius=1.25
  constraints (2):
    c: Coincident(g0,g-1)
    c: Diameter(g0) = 2.5
FEATURE [PartDesign::Hole] Hole004  label="Hole_InternThread001"
  BaseFeature = -> AdditiveLoft002
  ClaimChildren = false
  CustomThreadClearance = 0.3
  Depth = 7.5
  DepthType = 0
  Diameter = 8.8
  DrillForDepth = false
  DrillPoint = 1
  DrillPointAngle = 100
  Fit = 0
  FitJoin = 0
  HoleCutCountersinkAngle = 90
  HoleCutCustomValues = false
  HoleCutDepth = 0
  HoleCutDiameter = 9
  HoleCutType = 0
  InnerFit = 0
  InnerFitJoin = 0
  ModelThread = true
  NewSolid = false
  Profile = -> Sketch020
  Reversed = true
  Suppress = false
  Tapered = false
  TaperedAngle = 90
  ThreadClass = 0
  ThreadDepth = 7.5
  ThreadDepthType = 0
  ThreadDirection = 0
  ThreadFit = 0
  ThreadSize = 18
  ThreadType = 1
  Threaded = true
  TreeRank = 131
  UseCustomThreadClearance = true
  _ProfileBasedVersion = 1
  expr: Depth = Spec_PB3D_Tail_FCLinkBranch#<<params>>.balltail_thread_height + 2 * 1.5mm
FEATURE [PartDesign::Plane] DatumPlane003  label="DatumPlane_TailTop002"
  AttachmentOffset = pos=(0,0,24) rot=(0,0,1;0rad)
  Length = 26
  MapMode = 5
  MinimumLength = 10
  MinimumWidth = 10
  Placement = pos=(0,0,24) rot=(0,0,1;0rad)
  ResizeMode = 0
  Support = -> [XY_Plane012]
  TreeRank = 127
  Width = 30.0222
  expr: AttachmentOffset.Base.z = Spec_PB3D_Tail_FCLinkBranch#<<params>>.tail_top_height
FEATURE [Sketcher::SketchObject] Sketch021  label="Sketch_TailMid002"
  FullyConstrained = true
  MapMode = 5
  Support = -> [XY_Plane012]
  TreeRank = 126
  expr: Constraints[19] = Spec_PB3D_Tail_FCLinkBranch#<<params>>.tail_mid_width
  sketch-geometry (7):
    g0: LineSegment StartX=0 StartY=-15.0111 StartZ=0 EndX=13 EndY=-7.50555 EndZ=0
    g1: LineSegment StartX=13 StartY=-7.50555 StartZ=0 EndX=13 EndY=7.50555 EndZ=0
    g2: LineSegment StartX=13 StartY=7.50555 StartZ=0 EndX=0 EndY=15.0111 EndZ=0
    g3: LineSegment StartX=-8e-16 StartY=15.0111 StartZ=0 EndX=-13 EndY=7.50555 EndZ=0
    g4: LineSegment StartX=-13 StartY=7.50555 StartZ=0 EndX=-13 EndY=-7.50555 EndZ=0
    g5: LineSegment StartX=-13 StartY=-7.50555 StartZ=0 EndX=0 EndY=-15.0111 EndZ=0
    g6: Circle [constr] CenterX=0 CenterY=0 CenterZ=0 NormalX=0 NormalY=0 NormalZ=1 AngleXU=0 Radius=15.0111
  constraints (16):
    c: Coincident(g0,g1)
    c: Coincident(g1,g2)
    c: Coincident(g2,g3)
    c: Coincident(g3,g4)
    c: Coincident(g4,g5)
    c: Coincident(g5,g0)
    c: Equal(g0, g1-g5) x5
    c: PointOnObject(g0,g6)
    c: PointOnObject(g1,g6)
    c: PointOnObject(g2,g6)
    c: PointOnObject(g3,g6)
    c: PointOnObject(g4,g6)
    c: PointOnObject(g5,g6)
    c: Coincident(g6,g-1)
    c: PointOnObject(g5,g-2)
    c: DistanceX(g3,g1) = 26
FEATURE [Sketcher::SketchObject] Sketch022  label="Sketch_TailTop002"
  FullyConstrained = true
  MapMode = 5
  Placement = pos=(0,0,24) rot=(0,0,1;0rad)
  Support = -> [DatumPlane003]
  TreeRank = 128
  expr: Constraints[19] = Spec_PB3D_Tail_FCLinkBranch#<<params>>.tail_top_width
  sketch-geometry (7):
    g0: LineSegment StartX=1.1547 StartY=1e-16 StartZ=0 EndX=0.57735 EndY=1 EndZ=0
    g1: LineSegment StartX=0.57735 StartY=1 StartZ=0 EndX=-0.57735 EndY=1 EndZ=0
    g2: LineSegment StartX=-0.57735 StartY=1 StartZ=0 EndX=-1.1547 EndY=-1.1e-15 EndZ=0
    g3: LineSegment StartX=-1.1547 StartY=-1.1e-15 StartZ=0 EndX=-0.57735 EndY=-1 EndZ=0
    g4: LineSegment StartX=-0.57735 StartY=-1 StartZ=0 EndX=0.57735 EndY=-1 EndZ=0
    g5: LineSegment StartX=0.57735 StartY=-1 StartZ=0 EndX=1.1547 EndY=1e-16 EndZ=0
    g6: Circle [constr] CenterX=0 CenterY=0 CenterZ=0 NormalX=0 NormalY=0 NormalZ=1 AngleXU=0 Radius=1.1547
  constraints (16):
    c: Coincident(g0,g1)
    c: Coincident(g1,g2)
    c: Coincident(g2,g3)
    c: Coincident(g3,g4)
    c: Coincident(g4,g5)
    c: Coincident(g5,g0)
    c: Equal(g0, g1-g5) x5
    c: PointOnObject(g0,g6)
    c: PointOnObject(g1,g6)
    c: PointOnObject(g2,g6)
    c: PointOnObject(g3,g6)
    c: PointOnObject(g4,g6)
    c: PointOnObject(g5,g6)
    c: Coincident(g6,g-1)
    c: PointOnObject(g5,g-1)
    c: DistanceY(g4,g0) = 2
FEATURE [PartDesign::AdditiveLoft] AdditiveLoft003  label="AddLoft_HexTail_Top002"
  ClaimChildren = false
  Closed = false
  Fit = 0
  FitJoin = 0
  InnerFit = 0
  InnerFitJoin = 0
  NewSolid = false
  Profile = -> Sketch021
  Ruled = false
  Sections = -> [Sketch022]
  Suppress = false
  TreeRank = 134
  _ProfileBasedVersion = 1
FEATURE [Sketcher::SketchObject] Sketch023  label="Sketch_HoleLock002"
  FullyConstrained = true
  MapMode = 5
  Support = -> [XY_Plane012]
  TreeRank = 130
  expr: Constraints[1] = Spec_PB3D_Tail_FCLinkBranch#<<params>>.m2_hole_clear_diam
  sketch-geometry (1):
    g0: Circle CenterX=0 CenterY=0 CenterZ=0 NormalX=0 NormalY=0 NormalZ=1 AngleXU=0 Radius=1.25
  constraints (2):
    c: Coincident(g0,g-1)
    c: Diameter(g0) = 2.5
FEATURE [PartDesign::Hole] Hole005  label="Hole_InternThread002"
  BaseFeature = -> AdditiveLoft003
  ClaimChildren = false
  CustomThreadClearance = 0.2
  Depth = 7.5
  DepthType = 0
  Diameter = 8.7
  DrillForDepth = false
  DrillPoint = 1
  DrillPointAngle = 100
  Fit = 0
  FitJoin = 0
  HoleCutCountersinkAngle = 90
  HoleCutCustomValues = false
  HoleCutDepth = 0
  HoleCutDiameter = 9
  HoleCutType = 0
  InnerFit = 0
  InnerFitJoin = 0
  ModelThread = true
  NewSolid = false
  Profile = -> Sketch023
  Reversed = true
  Suppress = false
  Tapered = false
  TaperedAngle = 90
  ThreadClass = 0
  ThreadDepth = 7.5
  ThreadDepthType = 0
  ThreadDirection = 0
  ThreadFit = 0
  ThreadSize = 18
  ThreadType = 1
  Threaded = true
  TreeRank = 131
  UseCustomThreadClearance = true
  _ProfileBasedVersion = 1
  expr: Depth = Spec_PB3D_Tail_FCLinkBranch#<<params>>.balltail_thread_height + 2 * 1.5mm
FEATURE [Sketcher::SketchObject] Sketch024
  FullyConstrained = true
  MapMode = 5
  Support = -> [XY_Plane011]
  TreeRank = 136
  sketch-geometry (4):
    g0: LineSegment StartX=8.92376 StartY=0 StartZ=0 EndX=7.53812 EndY=0.8 EndZ=0
    g1: LineSegment StartX=7.53812 StartY=0.8 StartZ=0 EndX=7.53812 EndY=-0.8 EndZ=0
    g2: LineSegment StartX=7.53812 StartY=-0.8 StartZ=0 EndX=8.92376 EndY=0 EndZ=0
    g3: Circle [constr] CenterX=8 CenterY=0 CenterZ=0 NormalX=0 NormalY=0 NormalZ=1 AngleXU=0 Radius=0.92376
  constraints (12):
    c: Coincident(g0,g1)
    c: Coincident(g1,g2)
    c: Coincident(g2,g0)
    c: Equal(g0,g1)
    c: Equal(g0,g2)
    c: PointOnObject(g0,g3)
    c: PointOnObject(g1,g3)
    c: PointOnObject(g2,g3)
    c: PointOnObject(g3,g-1)
    c: PointOnObject(g2,g-1)
    c: DistanceY(g1,g0) = 1.6
    c: DistanceX(g-1,g3) = 8
FEATURE [PartDesign::Pocket] Pocket004
  BaseFeature = -> Hole004
  ClaimChildren = false
  Fit = 0
  FitJoin = 0
  InnerFit = 0
  InnerFitJoin = 0
  InnerTaperAngle = 0
  InnerTaperAngleRev = 0
  Length = 0.4
  Length2 = 100
  Linearize = true
  NewSolid = false
  Profile = -> Sketch024
  Reversed = true
  Suppress = false
  TreeRank = 137
  Type = 0
  _ProfileBasedVersion = 1
FEATURE [PartDesign::Body] Body008  label="Hex_Tail_Top_Tol03mm"
  AutoGroupSolids = false
  ExportMode = 0
  Group = -> [Sketch018,DatumPlane002,Sketch019,AdditiveLoft002,Sketch020,Hole004,Sketch024,Pocket004]
  Origin = -> Origin011
  Tip = -> Pocket004
  TreeRank = 133
  _ExportChildren = -> [DatumPlane002,AdditiveLoft002,Hole004,Pocket004]
  _GroupVersion = 1
FEATURE [Sketcher::SketchObject] Sketch025
  FullyConstrained = true
  MapMode = 5
  Support = -> [XY_Plane012]
  TreeRank = 138
  sketch-geometry (11):
    g0: LineSegment StartX=9.2 StartY=1.6 StartZ=0 EndX=8.4 EndY=1.6 EndZ=0
    g1: LineSegment StartX=8.4 StartY=1.6 StartZ=0 EndX=8.4 EndY=-1.6 EndZ=0
    g2: LineSegment StartX=8.4 StartY=-1.6 StartZ=0 EndX=9.2 EndY=-1.6 EndZ=0
    g3: LineSegment StartX=9.2 StartY=-1.6 StartZ=0 EndX=9.2 EndY=1.6 EndZ=0
    g4: LineSegment StartX=7.6 StartY=1.6 StartZ=0 EndX=6.8 EndY=1.6 EndZ=0
    g5: LineSegment StartX=6.8 StartY=1.6 StartZ=0 EndX=6.8 EndY=-1.59999 EndZ=0
    g6: LineSegment StartX=6.8 StartY=-1.59999 StartZ=0 EndX=7.6 EndY=-1.59999 EndZ=0
    g7: LineSegment StartX=7.6 StartY=-1.59999 StartZ=0 EndX=7.6 EndY=1.6 EndZ=0
    g8: LineSegment [constr] StartX=8.4 StartY=1.6 StartZ=0 EndX=7.6 EndY=1.6 EndZ=0
    g9: LineSegment [constr] StartX=8.4 StartY=-1.6 StartZ=0 EndX=7.6 EndY=-1.59999 EndZ=0
    g10: GeomPoint [constr] X=8 Y=0 Z=0
  constraints (29):
    c: Coincident(g0,g1)
    c: Coincident(g1,g2)
    c: Coincident(g2,g3)
    c: Coincident(g3,g0)
    c: Horizontal(g0)
    c: Horizontal(g2)
    c: Vertical(g1)
    c: Vertical(g3)
    c: Coincident(g4,g5)
    c: Coincident(g5,g6)
    c: Coincident(g6,g7)
    c: Coincident(g7,g4)
    c: Horizontal(g4)
    c: Horizontal(g6)
    c: Vertical(g5)
    c: Vertical(g7)
    c: Coincident(g8,g0)
    c: Coincident(g8,g4)
    c: Horizontal(g8)
    c: Coincident(g9,g1)
    c: Coincident(g9,g6)
    c: Equal(g9,g8)
    c: Equal(g0,g4)
    c: PointOnObject(g10,g-1)
    c: Symmetric(g1,g4,g10)
    c: DistanceX(g-1,g10) = 8
    c: DistanceX(g8,g8) = 0.8
    c: DistanceX(g0,g0) = 0.8
    c: DistanceY(g3,g3) = 3.2
FEATURE [PartDesign::Pocket] Pocket005
  BaseFeature = -> Hole005
  ClaimChildren = false
  Fit = 0
  FitJoin = 0
  InnerFit = 0
  InnerFitJoin = 0
  InnerTaperAngle = 0
  InnerTaperAngleRev = 0
  Length = 0.4
  Length2 = 100
  Linearize = true
  NewSolid = false
  Profile = -> Sketch025
  Reversed = true
  Suppress = false
  TreeRank = 139
  Type = 0
  _ProfileBasedVersion = 1
FEATURE [PartDesign::Body] Body009  label="Hex_Tail_Top_Tol02mm"
  AutoGroupSolids = false
  ExportMode = 0
  Group = -> [Sketch021,DatumPlane003,Sketch022,AdditiveLoft003,Sketch023,Hole005,Sketch025,Pocket005]
  Origin = -> Origin012
  Tip = -> Pocket005
  TreeRank = 135
  _ExportChildren = -> [DatumPlane003,AdditiveLoft003,Hole005,Pocket005]
  _GroupVersion = 1
FEATURE [App::Part] Part001  label="Hex_Tail_Part"
  ExportMode = 1
  Group = -> [Body005,Body006,Body007,Body008,Body009]
  Origin = -> Origin007
  TreeRank = 0
  _ExportChildren = -> [Body005,Body006,Body007,Body008,Body009]
  _GroupVersion = 1
FEATURE [Mesh::Feature] Mesh  label="Hex_Tail_Top_Tol03mm (Meshed)"
  TreeRank = 140
FEATURE [Mesh::Feature] Mesh001  label="Hex_Tail_Top_Tol02mm (Meshed)"
  TreeRank = 141
